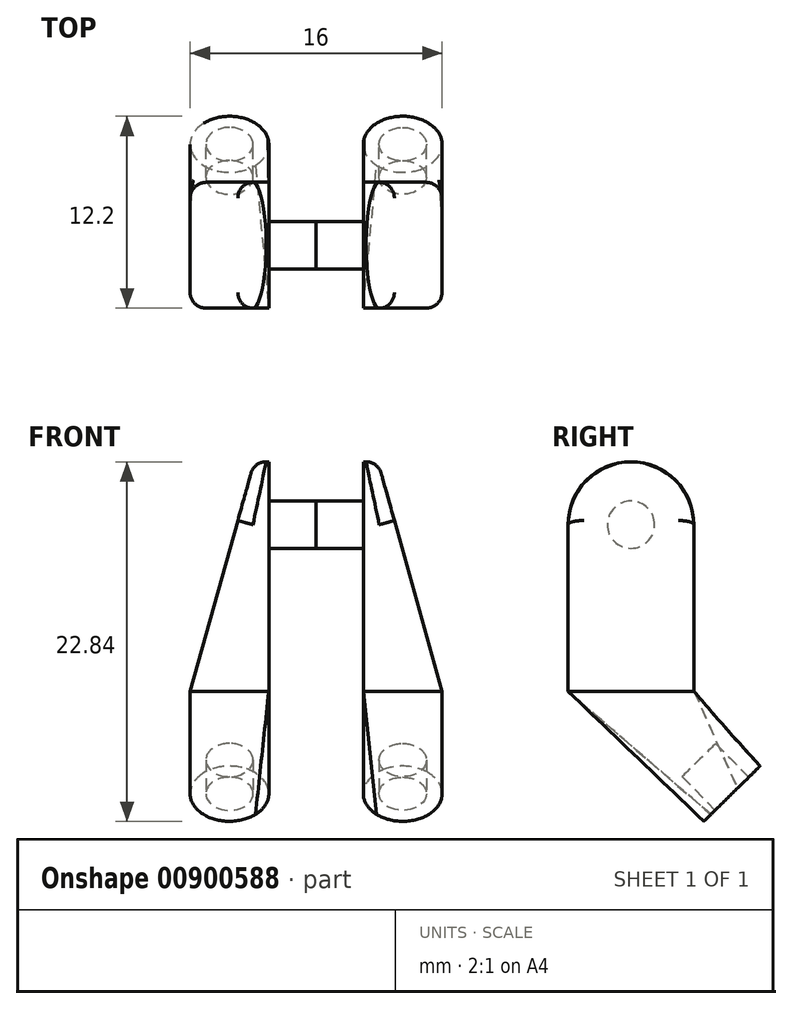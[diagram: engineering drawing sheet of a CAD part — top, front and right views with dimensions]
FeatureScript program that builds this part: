
annotation { "Feature Type Name" : "Feature", "Feature Type Description" : "" }
export const myFeature = defineFeature(function(context is Context, id is Id, definition is map)
    precondition{}
    {
        {
            var Q0;
            Q0=qCreatedBy(makeId("Right.planeOp"),FACE);
            var sketch = newSketch(context, id + "F0", { "sketchPlane" : qUnion([Q0])});
            skCircle(sketch, "E0", {"center": v(0, 0) * mm, "radius": 1.5 * mm});
            skCircle(sketch, "E1", {"center": v(0, 0) * mm, "radius": 4 * mm});
            skLineSegment(sketch, "E2.bottom", {"start": v(-4, 0) * mm, "end": v(4, 0) * mm});
            skLineSegment(sketch, "E2.top", {"start": v(-4, -10.57) * mm, "end": v(4, -10.57) * mm});
            skLineSegment(sketch, "E2.left", {"start": v(-4, 0) * mm, "end": v(-4, -10.57) * mm});
            skLineSegment(sketch, "E2.right", {"start": v(4, 0) * mm, "end": v(4, -10.57) * mm});
            skLineSegment(sketch, "E3", {"start": v(-4, -10.57) * mm, "end": v(4.38, -19.09) * mm, "construction": true});
            skLineSegment(sketch, "E4", {"start": v(4.38, -19.09) * mm, "end": v(8.45, -15.09) * mm, "construction": true});
            skLineSegment(sketch, "E5", {"start": v(8.45, -15.09) * mm, "end": v(4, -10.57) * mm, "construction": true});
            skLineSegment(sketch, "E6", {"start": v(6.42, -17.09) * mm, "end": v(3.4, -14.02) * mm, "construction": true});
            skSolve(sketch);
        }
        {
            var Q0;
            {var subQ0=sQuery(id+"F0.wireOp",EDGE,"E2.bottom");var subQ1=sQuery(id+"F0.wireOp",EDGE,"E0");var subQ2=makeQuery(id+"F0.imprint","INTERSECT",VERTEX,{"disambiguationData":[OD(0.0)],"derivedFrom":[subQ1,subQ0]});Q0=makeQuery(id+"F0.imprint","IMPRINT",FACE,{"disambiguationData":[TD([[makeQuery(id+"F0.imprint","IMPRINT",EDGE,{"disambiguationData":[TD([[subQ2,1.0]])],"derivedFrom":subQ1}),1.0]])]});}
            var Q1;
            {var subQ0=sQuery(id+"F0.wireOp",EDGE,"E2.bottom");var subQ1=sQuery(id+"F0.wireOp",EDGE,"E0");var subQ2=makeQuery(id+"F0.imprint","INTERSECT",VERTEX,{"disambiguationData":[OD(0.0)],"derivedFrom":[subQ1,subQ0]});Q1=makeQuery(id+"F0.imprint","IMPRINT",FACE,{"disambiguationData":[TD([[makeQuery(id+"F0.imprint","IMPRINT",EDGE,{"disambiguationData":[TD([[subQ2,-1.0]])],"derivedFrom":subQ1}),1.0]])]});}
            extrude(context, id + "F1", {"entities" : qUnion([Q0, Q1]), "oppositeDirection" : true, "depth" : 3 * mm, "offsetDistance" : 25 * mm});
        }
        {
            var Q0;
            {var subQ0=sQuery(id+"F0.wireOp",EDGE,"E2.bottom");var subQ1=sQuery(id+"F0.wireOp",EDGE,"E0");var subQ2=makeQuery(id+"F0.imprint","INTERSECT",VERTEX,{"disambiguationData":[OD(0.0)],"derivedFrom":[subQ1,subQ0]});Q0=makeQuery(id+"F0.imprint","IMPRINT",FACE,{"disambiguationData":[TD([[makeQuery(id+"F0.imprint","IMPRINT",EDGE,{"disambiguationData":[TD([[subQ2,-1.0]])],"derivedFrom":subQ1}),-1.0]])]});}
            var Q1;
            {var subQ0=sQuery(id+"F0.wireOp",EDGE,"E2.bottom");var subQ1=sQuery(id+"F0.wireOp",EDGE,"E0");var subQ2=makeQuery(id+"F0.imprint","INTERSECT",VERTEX,{"disambiguationData":[OD(0.0)],"derivedFrom":[subQ1,subQ0]});Q1=makeQuery(id+"F0.imprint","IMPRINT",FACE,{"disambiguationData":[TD([[makeQuery(id+"F0.imprint","IMPRINT",EDGE,{"disambiguationData":[TD([[subQ2,-1.0]])],"derivedFrom":subQ1}),1.0]])]});}
            var Q2;
            {var subQ0=sQuery(id+"F0.wireOp",EDGE,"E2.bottom");var subQ1=sQuery(id+"F0.wireOp",EDGE,"E0");var subQ2=makeQuery(id+"F0.imprint","INTERSECT",VERTEX,{"disambiguationData":[OD(0.0)],"derivedFrom":[subQ1,subQ0]});Q2=makeQuery(id+"F0.imprint","IMPRINT",FACE,{"disambiguationData":[TD([[makeQuery(id+"F0.imprint","IMPRINT",EDGE,{"disambiguationData":[TD([[subQ2,1.0]])],"derivedFrom":subQ1}),1.0]])]});}
            var Q3;
            Q3=makeQuery(id+"F0.imprint","IMPRINT",FACE,{"disambiguationData":[TD([[makeQuery(id+"F0.imprint","IMPRINT",EDGE,{"derivedFrom":sQuery(id+"F0.wireOp",EDGE,"E2.top")}),1.0]])]});
            var Q4;
            {var subQ0=sQuery(id+"F0.wireOp",EDGE,"E2.bottom");var subQ1=sQuery(id+"F0.wireOp",EDGE,"E0");var subQ2=makeQuery(id+"F0.imprint","INTERSECT",VERTEX,{"disambiguationData":[OD(0.0)],"derivedFrom":[subQ1,subQ0]});Q4=makeQuery(id+"F0.imprint","IMPRINT",FACE,{"disambiguationData":[TD([[makeQuery(id+"F0.imprint","IMPRINT",EDGE,{"disambiguationData":[TD([[subQ2,1.0]])],"derivedFrom":subQ1}),-1.0]])]});}
            extrude(context, id + "F2", {"entities" : qUnion([Q0, Q1, Q2, Q3, Q4]), "operationType" : NewBodyOperationType.ADD, "depth" : 5 * mm, "offsetDistance" : 25 * mm});
        }
        {
            var Q0;
            Q0=makeQuery(id+"F2.opExtrude","SWEPT_FACE",FACE,{"disambiguationData":[OSD([sQuery(id+"F0.wireOp",EDGE,"E2.right")])]});
            var sketch = newSketch(context, id + "F3", { "sketchPlane" : qUnion([Q0])});
            skLineSegment(sketch, "E7", {"start": v(-5, -10.57) * mm, "end": v(0, 7.33) * mm});
            skLineSegment(sketch, "E8", {"start": v(0, 7.33) * mm, "end": v(-7.46, 7.33) * mm});
            skLineSegment(sketch, "E9", {"start": v(-7.46, 7.33) * mm, "end": v(-5, -10.57) * mm});
            skSolve(sketch);
        }
        {
            var Q0;
            Q0 = qSketchRegion(id + "F3", true);
            extrude(context, id + "F4", {"entities" : qUnion([Q0]), "operationType" : NewBodyOperationType.REMOVE, "oppositeDirection" : true, "depth" : 25 * mm, "offsetDistance" : 25 * mm});
        }
        {
            var Q0;
            Q0=makeQuery(id+"F4.boolean.opBoolean","COPY",EDGE,{"derivedFrom":makeQuery(id+"F4.opExtrude","CAP_EDGE",EDGE,{"disambiguationData":[OSD([sQuery(id+"F3.wireOp",EDGE,"E7")])],"isStart":true})});
            var Q1;
            Q1=makeQuery(id+"F4.boolean.opBoolean","INTERSECT",EDGE,{"derivedFrom":[makeQuery(id+"F2.opExtrude","SWEPT_FACE",FACE,{"disambiguationData":[OSD([sQuery(id+"F0.wireOp",EDGE,"E1")])]}),makeQuery(id+"F4.opExtrude","SWEPT_FACE",FACE,{"disambiguationData":[OSD([sQuery(id+"F3.wireOp",EDGE,"E7")])]})]});
            var Q2;
            Q2=makeQuery(id+"F4.boolean.opBoolean","INTERSECT",EDGE,{"derivedFrom":[makeQuery(id+"F2.opExtrude","SWEPT_FACE",FACE,{"disambiguationData":[OSD([sQuery(id+"F0.wireOp",EDGE,"E2.left")])]}),makeQuery(id+"F4.opExtrude","SWEPT_FACE",FACE,{"disambiguationData":[OSD([sQuery(id+"F3.wireOp",EDGE,"E7")])]})]});
            fillet(context, id + "F5", {"entities" : qUnion([Q0, Q1, Q2]), "radius" : 1 * mm, "tangentPropagation" : true, "allowEdgeOverflow" : false});
        }
        {
            var Q0;
            Q0=sQuery(id+"F0.wireOp",VERTEX,"E6.start");
            var Q1;
            Q1=sQuery(id+"F0.wireOp",EDGE,"E6");
            cPlane(context, id + "F6", {"entities" : qUnion([Q0, Q1]), "cplaneType" : CPlaneType.LINE_POINT, "offset" : 25 * mm, "width" : 150 * mm, "height" : 150 * mm});
        }
        {
            var Q0;
            Q0=qCreatedBy(id+"F6.planeOp",FACE);
            var sketch = newSketch(context, id + "F7", { "sketchPlane" : qUnion([Q0])});
            skLineSegment(sketch, "E10", {"start": v(0, -7.42) * mm, "end": v(5.93, -7.42) * mm, "construction": true});
            skCircle(sketch, "E11", {"center": v(2.5, -7.42) * mm, "radius": 2.5 * mm});
            skSolve(sketch);
        }
        {
            var Q1;
            Q1=makeQuery(id+"F2.opExtrude","SWEPT_FACE",FACE,{"disambiguationData":[OSD([sQuery(id+"F0.wireOp",EDGE,"E2.top")])]});
            var Q2;
            Q2=makeQuery(id+"F7.imprint","IMPRINT",FACE,{"disambiguationData":[TD([[makeQuery(id+"F7.imprint","IMPRINT",EDGE,{"derivedFrom":sQuery(id+"F7.wireOp",EDGE,"E11")}),1.0]])]});
            loft(context, id + "F8", {"operationType" : NewBodyOperationType.ADD, "sheetProfilesArray" : [{ "sheetProfileEntities" : qUnion([Q1]) }, { "sheetProfileEntities" : qUnion([Q2]) }]});
        }
        {
            var Q0;
            Q0=makeQuery(id+"F8.opLoft","CAP_FACE",FACE,{"disambiguationData":[OSD([makeQuery(id+"F7.imprint","IMPRINT",FACE,{"disambiguationData":[TD([[makeQuery(id+"F7.imprint","IMPRINT",EDGE,{"derivedFrom":sQuery(id+"F7.wireOp",EDGE,"E11")}),1.0]])]})])],"isStart":true});
            var sketch = newSketch(context, id + "F9", { "sketchPlane" : qUnion([Q0])});
            skFitSpline(sketch, "E12.0", {"points": [v(5.93, 8.1) * mm, v(5.81, 8.7) * mm, v(5.25, 9.84) * mm, v(4.2, 10.54) * mm, v(3.62, 10.73) * mm], "construction": true});
            skFitSpline(sketch, "E12.1", {"points": [v(0.2, 10.05) * mm, v(-0.27, 9.65) * mm, v(-0.97, 8.6) * mm, v(-1.05, 7.34) * mm, v(-0.93, 6.74) * mm], "construction": true});
            skFitSpline(sketch, "E12.2", {"points": [v(-0.93, 6.74) * mm, v(-0.81, 6.14) * mm, v(-0.25, 5) * mm, v(0.8, 4.3) * mm, v(1.38, 4.1) * mm], "construction": true});
            skFitSpline(sketch, "E12.3", {"points": [v(3.62, 10.73) * mm, v(3.05, 10.93) * mm, v(1.78, 11.01) * mm, v(0.65, 10.45) * mm, v(0.2, 10.05) * mm], "construction": true});
            skFitSpline(sketch, "E12.4", {"points": [v(1.38, 4.1) * mm, v(1.95, 3.9) * mm, v(3.22, 3.83) * mm, v(4.35, 4.39) * mm, v(4.8, 4.79) * mm], "construction": true});
            skFitSpline(sketch, "E12.5", {"points": [v(4.8, 4.79) * mm, v(5.27, 5.2) * mm, v(5.97, 6.24) * mm, v(6.05, 7.5) * mm, v(5.93, 8.1) * mm], "construction": true});
            skCircle(sketch, "E13", {"center": v(2.5, 7.42) * mm, "radius": 1.5 * mm});
            skLineSegment(sketch, "E14", {"start": v(1.38, 4.1) * mm, "end": v(3.62, 10.73) * mm, "construction": true});
            skSolve(sketch);
        }
        {
            var Q0;
            Q0 = qSketchRegion(id + "F9", true);
            extrude(context, id + "F10", {"entities" : qUnion([Q0]), "operationType" : NewBodyOperationType.REMOVE, "oppositeDirection" : true, "depth" : 3 * mm, "offsetDistance" : 25 * mm});
        }
        {
            var Q0;
            Q0=makeQuery(id+"F1.opExtrude","SWEPT_BODY",BODY,{"disambiguationData":[OSD([sQuery(id+"F0.wireOp",EDGE,"E0")])]});
            var Q1;
            Q1=makeQuery(id+"F1.opExtrude","CAP_FACE",FACE,{"disambiguationData":[OSD([sQuery(id+"F0.wireOp",EDGE,"E0")])],"isStart":false});
            mirror(context, id + "F11", {"entities" : qUnion([Q0]), "mirrorPlane" : qUnion([Q1])});
        }
    });
